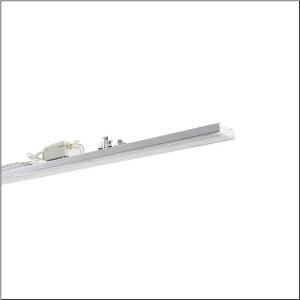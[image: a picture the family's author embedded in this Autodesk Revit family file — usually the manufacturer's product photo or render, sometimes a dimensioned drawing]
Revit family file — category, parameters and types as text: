
# Revit family: licross_21_recessed_ho_52te12dn4fxm3s4
name_source: partatom
category: Lighting Fixtures
units: mm (PartAtom-declared; Revit-internal decimal feet)

## family parameters
Cut with Voids When Loaded = No
Host = Face
Light Source = No
Part Type = Normal
Room Calculation Point = No
Round Connector Dimension = Use Diameter
Shared = No

## types (1)
- --- (1 x LED, 930 lm, 7.5 W, 4000K)
    Apparent Load = 8 VA
    CIE Flux Codes = 69 91 98 100 100
    Color Rendering = 80
    Color Temperature = 4000K
    Default Elevation = 1800 mm
    Description = Licross 21 Recessed HO, luminaire insert, of sheet steel, galvanised, coil coated, white, length: 1.500mm, width: 66mm, height: 67mm, LED rated luminous flux: 15.000lm, light colour: 840, SDCM (Standard Deviation of Colour Matching)MacAdam ≤ 3 SDCM (initial), control gear: DALI 2, with plug, 6-pole, with phase selection, for trunking rail, 9 or 11-core, mains connection: 220..240V, AC, 50/60Hz, rated input power: 88W, internal wiring halogen-free, for emergency light function, for trunking rail, 9-/11-core, converter,control gear: single battery element, battery: LiFePO4, 9Ah, primary optical cover: cover, of PMMA, light emission: direct distribution, primary light characteristic: symmetric, protection rating (complete): IP54, insulation class (complete): insulation class I (protective earthing), certification: CE, UKCA, protection symbol: D if used in an environment with non-conductive dust loads with corresponding accessories, impact resistance: IK06, permissible ambient temperature for indoor applications: +5..+30°C, standard: EN 60598-2-22, LABS conformity tested according to VDMA 24364:2018-05, reducing of maximum allowable ambient temperature of 5°C with ceiling mounting, corresponds to IFS (International Featured Standards) requirements for safety and quality in the food industry, The light source and the operating device comply with the requirements of the Ecodesign Regulation (EU) 2019/2020 and are replaceable in accordance with this regulation, packaging unit: 1 piece
    Height = 58 mm
    Lamp = 1 x LED
    Lamp Light Flux = 930 lm
    Lamp Power = 7.5 W
    Lamp count = 1
    Length = 1500 mm
    Luminous efficacy = 124 lm/W
    Manufacturer = Siteco
    ModVariant = No
    Model = 52TE12DN4FXM3S4
    Mounting Place = Ceiling
    Mounting Type = Pendant
    Number of Poles = 1
    OnlyDefault = Yes
    Power Factor = 1
    Product Name = Licross 21 Recessed HO
    Product group = luminaire insert | ceiling pendant
    ProductGroupID = 901
    Protection Class = Protection class I
    Protection Degree = IP 54
    RLX_Detail_Level = 1
    RLX_Emergency_Light_Flux = 0 lm
    RLX_Emergency_Type = 0
    RLX_Emergency_Type_DB = No
    RlxData = <blob elided: 25445 chars, md5=aefa90de>
    Socket = socket
    Standby Power = 0 W
    System Light Flux = 930 lm
    System Power = 8 W
    Type Comments = : emergency light operation: 3 h
    Type Image = l_1296930.jpg
    URL = http://relux.com
    VarID = @adj_110773
    Voltage = 0 V
    Weight = 0.00 kg
    Width = 66 mm

## geometry (parser evidence)
native form markers: Blend x4, Sweep x10
no freeform markers — native parametric forms only
